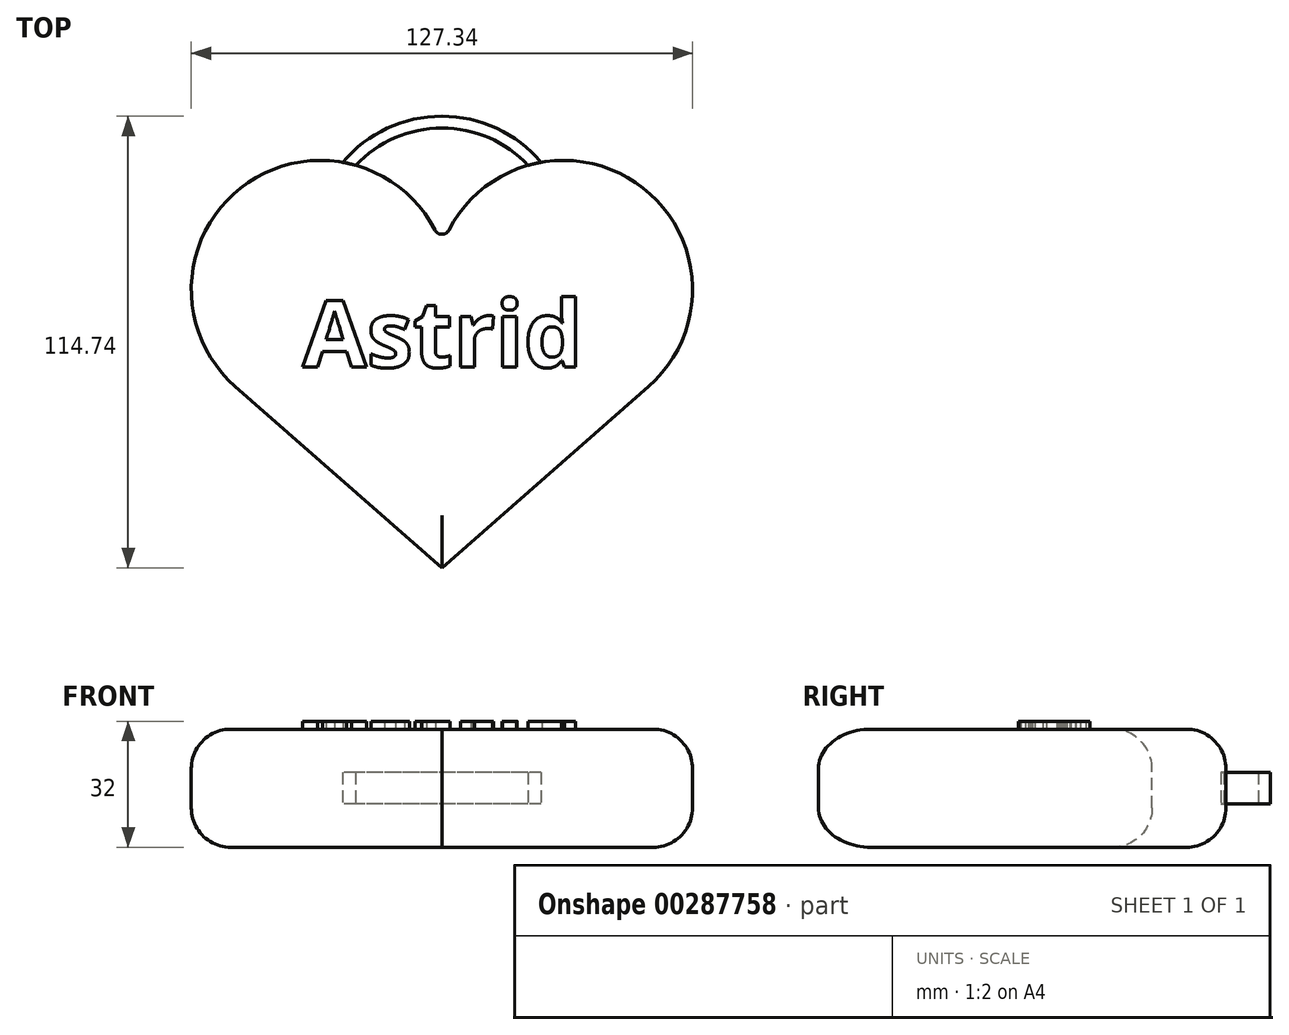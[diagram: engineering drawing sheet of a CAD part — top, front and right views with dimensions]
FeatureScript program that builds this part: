
annotation { "Feature Type Name" : "Feature", "Feature Type Description" : "" }
export const myFeature = defineFeature(function(context is Context, id is Id, definition is map)
    precondition{}
    {
        {
            var Q0;
            Q0=qCreatedBy(makeId("Top.planeOp"),FACE);
            var sketch = newSketch(context, id + "F0", { "sketchPlane" : qUnion([Q0])});
            skLineSegment(sketch, "E0", {"start": v(52.51, 0) * mm, "end": v(0, -46.08) * mm});
            skLineSegment(sketch, "E1", {"start": v(-52.51, 0) * mm, "end": v(0, -46.08) * mm});
            skArc(sketch, "E2", {"start": v(52.51, 0) * mm, "mid": v(49.3, 51.77) * mm, "end": v(0, 35.66) * mm});
            skArc(sketch, "E3", {"start": v(-52.51, 0) * mm, "mid": v(-49.3, 51.77) * mm, "end": v(0, 35.66) * mm});
            skLineSegment(sketch, "E4", {"start": v(-52.51, 0) * mm, "end": v(-52.51, 0) * mm});
            skSolve(sketch);
        }
        {
            var Q0;
            Q0=makeQuery(id+"F0.imprint","IMPRINT",FACE,{"disambiguationData":[TD([[makeQuery(id+"F0.imprint","IMPRINT",EDGE,{"derivedFrom":sQuery(id+"F0.wireOp",EDGE,"E0")}),-1.0]])]});
            extrude(context, id + "F1", {"entities" : qUnion([Q0]), "depth" : 30 * mm});
        }
        {
            var Q0;
            Q0=qCreatedBy(makeId("Top.planeOp"),FACE);
            var Q1;
            Q1=makeQuery(id+"F1.opExtrude","CAP_FACE",FACE,{"disambiguationData":[OSD([sQuery(id+"F0.wireOp",EDGE,"E0"),sQuery(id+"F0.wireOp",EDGE,"E1"),sQuery(id+"F0.wireOp",EDGE,"E2"),sQuery(id+"F0.wireOp",EDGE,"E3")])],"isStart":false});
            cPlane(context, id + "F2", {"entities" : qUnion([Q0, Q1]), "cplaneType" : CPlaneType.MID_PLANE, "offset" : 25 * mm, "width" : 150 * mm, "height" : 150 * mm});
        }
        {
            var Q0;
            Q0=qCreatedBy(id+"F2.planeOp",FACE);
            var sketch = newSketch(context, id + "F3", { "sketchPlane" : qUnion([Q0])});
            skArc(sketch, "E5", {"start": v(21.89, 56.18) * mm, "mid": v(0, 65.66) * mm, "end": v(-21.89, 56.18) * mm});
            skArc(sketch, "E6.0", {"start": v(25.22, 56.94) * mm, "mid": v(0, 68.66) * mm, "end": v(-25.22, 56.94) * mm});
            skArc(sketch, "E7.0", {"start": v(-52.51, 0) * mm, "mid": v(-49.3, 51.77) * mm, "end": v(0, 35.66) * mm});
            skArc(sketch, "E8.0", {"start": v(52.51, 0) * mm, "mid": v(49.3, 51.77) * mm, "end": v(0, 35.66) * mm});
            skSolve(sketch);
        }
        {
            var Q0;
            {var subQ0=sQuery(id+"F3.wireOp",EDGE,"E5");Q0=makeQuery(id+"F3.imprint","IMPRINT",FACE,{"disambiguationData":[TD([[makeQuery(id+"F3.imprint","IMPRINT",EDGE,{"derivedFrom":subQ0}),-1.0]])]});}
            extrude(context, id + "F4", {"entities" : qUnion([Q0]), "operationType" : NewBodyOperationType.ADD, "depth" : 4 * mm, "hasSecondDirection" : true, "secondDirectionOppositeDirection" : true, "secondDirectionDepth" : 4 * mm});
        }
        {
            var Q0;
            Q0=makeQuery(id+"F1.opExtrude","SWEPT_EDGE",EDGE,{"disambiguationData":[OSD([sQuery(id+"F0.wireOp",EDGE,"E2"),sQuery(id+"F0.wireOp",EDGE,"E3")])]});
            fillet(context, id + "F5", {"entities" : qUnion([Q0]), "radius" : 2 * mm, "tangentPropagation" : true, "allowEdgeOverflow" : false});
        }
        {
            var Q0;
            Q0=makeQuery(id+"F1.opExtrude","CAP_EDGE",EDGE,{"disambiguationData":[OSD([sQuery(id+"F0.wireOp",EDGE,"E3")])],"isStart":false});
            var Q1;
            Q1=makeQuery(id+"F1.opExtrude","CAP_EDGE",EDGE,{"disambiguationData":[OSD([sQuery(id+"F0.wireOp",EDGE,"E3")])],"isStart":true});
            fillet(context, id + "F6", {"entities" : qUnion([Q0, Q1]), "radius" : 10 * mm, "tangentPropagation" : true, "allowEdgeOverflow" : false});
        }
        {
            var Q0;
            Q0=makeQuery(id+"F1.opExtrude","CAP_FACE",FACE,{"disambiguationData":[OSD([sQuery(id+"F0.wireOp",EDGE,"E0"),sQuery(id+"F0.wireOp",EDGE,"E1"),sQuery(id+"F0.wireOp",EDGE,"E2"),sQuery(id+"F0.wireOp",EDGE,"E3")])],"isStart":false});
            var sketch = newSketch(context, id + "F7", { "sketchPlane" : qUnion([Q0])});
            skText(sketch, "E9", { "text": "Astrid", "fontName": "OpenSans-Bold.ttf"});
            const initialGuessF7  = {"E9": [-0.03541, 0.00488, 1, 0, 0.017]};
            skSetInitialGuess(sketch, initialGuessF7);
            skSolve(sketch);
        }
        {
            var Q0;
            Q0=makeQuery(id+"F7.imprint","IMPRINT",FACE,{"disambiguationData":[TD([[makeQuery(id+"F7.imprint","IMPRINT",EDGE,{"derivedFrom":sQuery(id+"F7.wireOp",EDGE,"E9.sketch_text.stroke-0")}),-1.0]])]});
            var Q1;
            Q1=makeQuery(id+"F7.imprint","IMPRINT",FACE,{"disambiguationData":[TD([[makeQuery(id+"F7.imprint","IMPRINT",EDGE,{"derivedFrom":sQuery(id+"F7.wireOp",EDGE,"E9.sketch_text.stroke-12")}),-1.0]])]});
            var Q2;
            Q2=makeQuery(id+"F7.imprint","IMPRINT",FACE,{"disambiguationData":[TD([[makeQuery(id+"F7.imprint","IMPRINT",EDGE,{"derivedFrom":sQuery(id+"F7.wireOp",EDGE,"E9.sketch_text.stroke-38")}),-1.0]])]});
            var Q3;
            Q3=makeQuery(id+"F7.imprint","IMPRINT",FACE,{"disambiguationData":[TD([[makeQuery(id+"F7.imprint","IMPRINT",EDGE,{"derivedFrom":sQuery(id+"F7.wireOp",EDGE,"E9.sketch_text.stroke-56")}),-1.0]])]});
            var Q4;
            Q4=makeQuery(id+"F7.imprint","IMPRINT",FACE,{"disambiguationData":[TD([[makeQuery(id+"F7.imprint","IMPRINT",EDGE,{"derivedFrom":sQuery(id+"F7.wireOp",EDGE,"E9.sketch_text.stroke-74")}),-1.0]])]});
            var Q5;
            Q5=makeQuery(id+"F7.imprint","IMPRINT",FACE,{"disambiguationData":[TD([[makeQuery(id+"F7.imprint","IMPRINT",EDGE,{"derivedFrom":sQuery(id+"F7.wireOp",EDGE,"E9.sketch_text.stroke-69")}),-1.0]])]});
            var Q6;
            Q6=makeQuery(id+"F7.imprint","IMPRINT",FACE,{"disambiguationData":[TD([[makeQuery(id+"F7.imprint","IMPRINT",EDGE,{"derivedFrom":sQuery(id+"F7.wireOp",EDGE,"E9.sketch_text.stroke-78")}),-1.0]])]});
            extrude(context, id + "F8", {"entities" : qUnion([Q0, Q1, Q2, Q3, Q4, Q5, Q6]), "operationType" : NewBodyOperationType.ADD, "depth" : 2 * mm});
        }
    });
